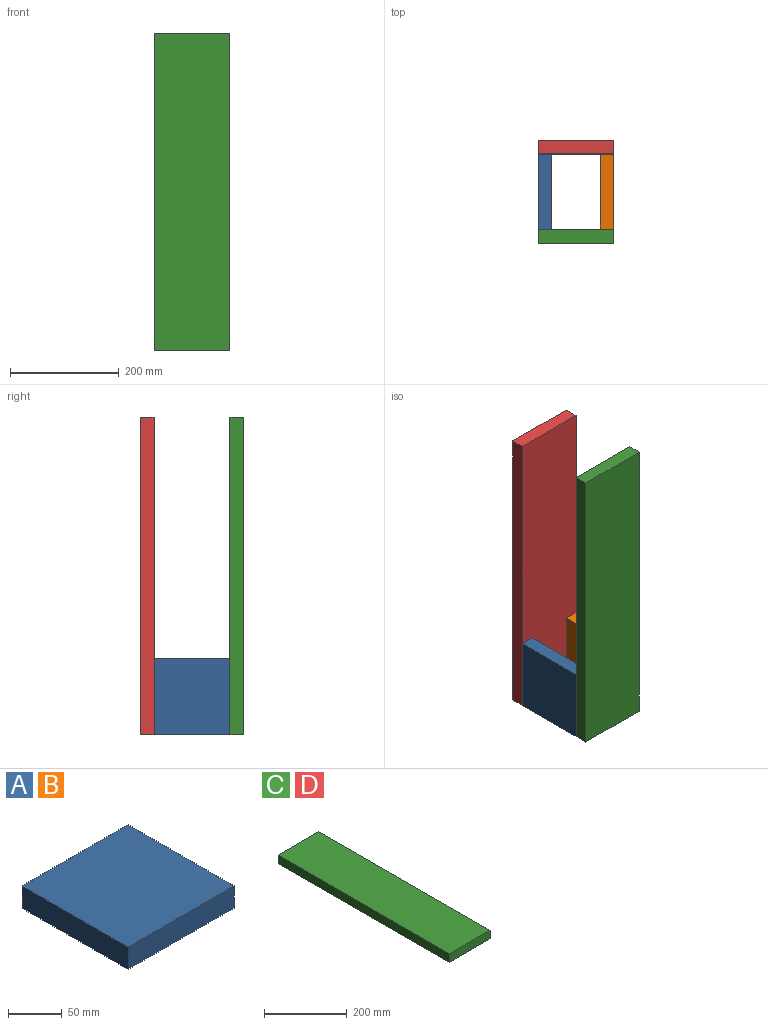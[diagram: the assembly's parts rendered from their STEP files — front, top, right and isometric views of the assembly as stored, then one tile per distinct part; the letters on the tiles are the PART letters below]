
ASSEMBLY  parts=4 mates=9
PART A: 6 faces, bbox 139.7x139.7x25.4 mm
  f0: plane 139.7x25.4mm, normal (0,1,0), area 3548.4mm2, adj f1,f3,f4,f5
  f1: plane 139.7x25.4mm, normal (-1,0,0), area 3548.4mm2, adj f0,f2,f4,f5
  f2: plane 139.7x25.4mm, normal (0,-1,0), area 3548.4mm2, adj f1,f3,f4,f5
  f3: plane 139.7x25.4mm, normal (1,0,0), area 3548.4mm2, adj f0,f2,f4,f5
  f4: plane 139.7x139.7mm, normal (0,0,1), area 19516.1mm2, adj f0,f1,f2,f3
  f5: plane 139.7x139.7mm, normal (0,0,-1), area 19516.1mm2, adj f0,f1,f2,f3
PART B: same geometry as A
PART C: 6 faces, bbox 139.7x584.2x25.4 mm
  f0: plane 139.7x25.4mm, normal (0,1,0), area 3548.4mm2, adj f1,f3,f4,f5
  f1: plane 584.2x25.4mm, normal (-1,0,0), area 14838.7mm2, adj f0,f2,f4,f5
  f2: plane 139.7x25.4mm, normal (0,-1,0), area 3548.4mm2, adj f1,f3,f4,f5
  f3: plane 584.2x25.4mm, normal (1,0,0), area 14838.7mm2, adj f0,f2,f4,f5
  f4: plane 584.2x139.7mm, normal (0,0,1), area 81612.7mm2, adj f0,f1,f2,f3
  f5: plane 584.2x139.7mm, normal (0,0,-1), area 81612.7mm2, adj f0,f1,f2,f3
PART D: same geometry as C
PLACE A rot(axis=(0.58,0.58,0.58),120deg) t=(-214.62,55.07,-365.38)mm
PLACE B rot(axis=(0.58,-0.58,-0.58),120deg) t=(-74.92,194.77,-365.38)mm
PLACE C rot(axis=(-1,0,0),90deg) t=(-214.62,29.67,-505.08)mm
PLACE D rot(axis=(0,-0.71,0.71),180deg) t=(-74.92,220.17,-505.08)mm
MATE planar C.f0 <-> D.f0  axis (0,0,-1) through (-74.92,29.67,-505.08)mm
MATE planar B.f5 <-> C.f3  axis (1,0,0) through (-74.92,55.07,-505.08)mm
MATE planar C.f0 <-> B.f2  axis (0,0,-1) through (-144.77,42.37,-505.08)mm
MATE planar B.f5 <-> D.f1  axis (1,0,0) through (-74.92,124.92,-435.23)mm
MATE planar A.f1 <-> C.f4  axis (0,-1,0) through (-201.92,55.07,-435.23)mm
MATE planar A.f5 <-> C.f1  axis (-1,0,0) through (-214.62,124.92,-435.23)mm
MATE planar B.f2 <-> A.f2  axis (0,0,-1) through (-100.32,194.77,-505.08)mm
MATE planar C.f4 <-> B.f3  axis (0,1,0) through (-144.77,55.07,-212.98)mm
MATE planar D.f4 <-> B.f1  axis (0,-1,0) through (-74.92,194.77,-212.98)mm
